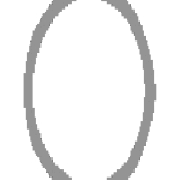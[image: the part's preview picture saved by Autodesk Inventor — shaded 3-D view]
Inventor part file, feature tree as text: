
AUTODESK INVENTOR PART (.ipt)
format: ipt  version: 2021 (Build 250183000, 183)  size: 109,568 bytes
history: native  units: in
note: dims shown in document units (in); Inventor stores cm internally (conversion verified against a paired STEP export)
features: other x4, sketch x3, plane x1
ambient origin geometry x8: Origin, YZ Plane, XZ Plane, XY Plane, X Axis, Y Axis, Z Axis, Center Point
bodies: Solid1 (feature_tree), Body (feature_tree)
feature tree (8):
  other  "Driven Length"
  other  "Frame Generator"
  other  "Start Plane"
  other  "End Plane"
  sketch  "Sketch"  dims[d2=23.8537in d4=-0.0in d5=23.8537in d6=0.12in d7=0.0in d8=90.0deg d9=23.8537in]
  sketch  "Sketch2"  dims[d0=1.0in]
  plane  "Work Plane3"
  sketch  "Sketch3"  dims[d1=0.065in]
